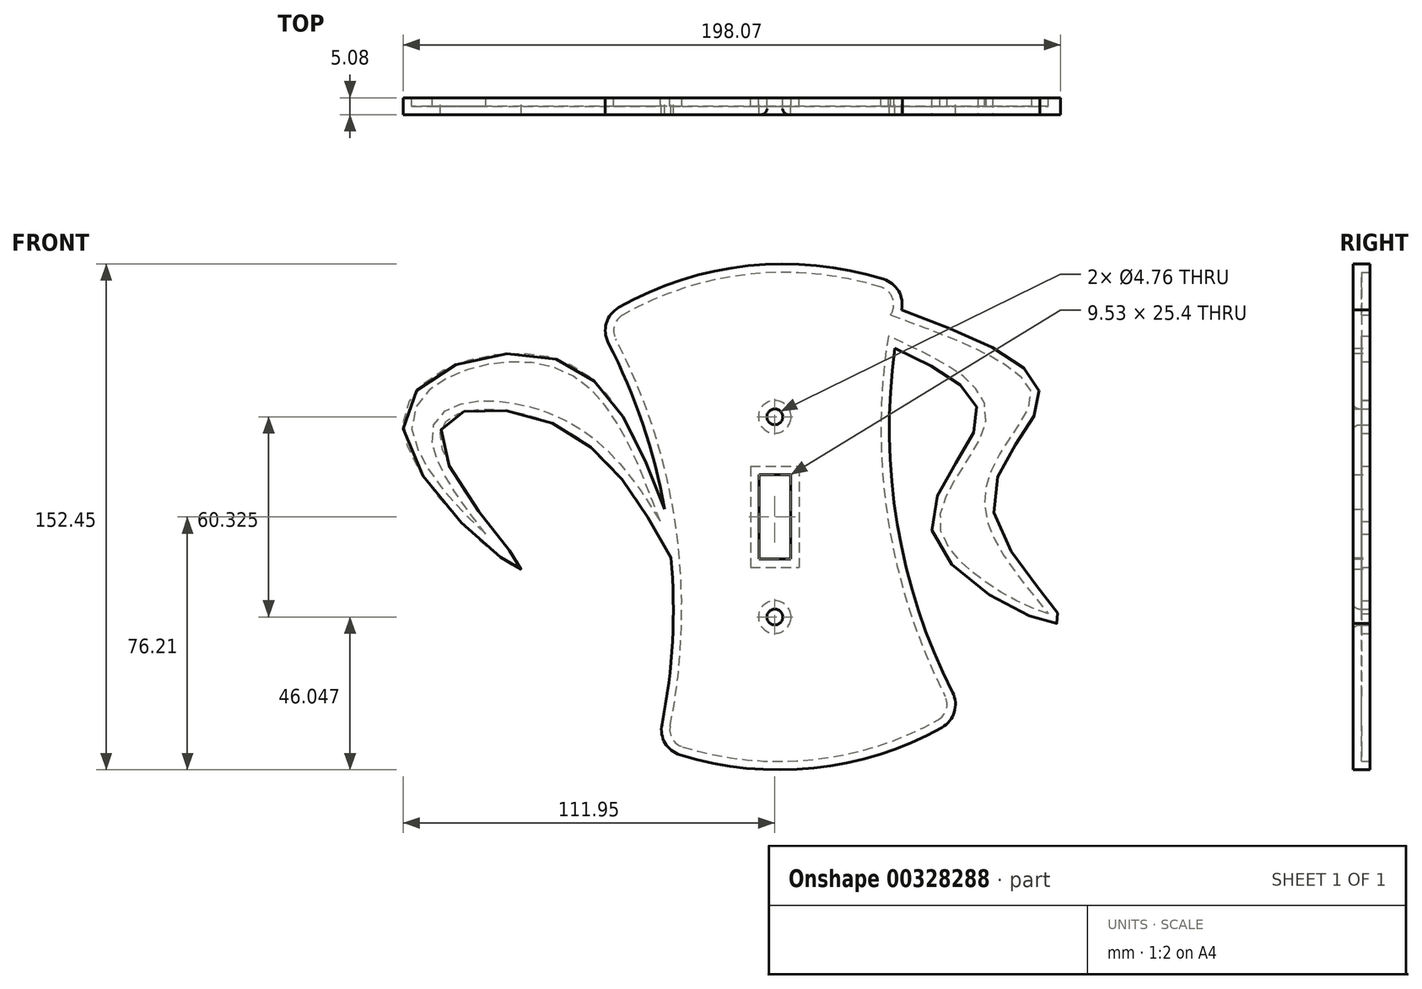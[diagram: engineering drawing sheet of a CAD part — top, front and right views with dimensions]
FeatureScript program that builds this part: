
annotation { "Feature Type Name" : "Feature", "Feature Type Description" : "" }
export const myFeature = defineFeature(function(context is Context, id is Id, definition is map)
    precondition{}
    {
        {
            var Q0;
            Q0=qCreatedBy(makeId("Front.planeOp"),FACE);
            var sketch = newSketch(context, id + "F0", { "sketchPlane" : qUnion([Q0])});
            skArc(sketch, "E0", {"start": v(-34, -62.51) * mm, "mid": v(-30.83, -37.47) * mm, "end": v(-31.28, -12.22) * mm});
            skArc(sketch, "E1", {"start": v(32.8, 71.63) * mm, "mid": v(-8, 75.67) * mm, "end": v(-47.03, 63.1) * mm});
            skArc(sketch, "E2", {"start": v(-28.56, -71.7) * mm, "mid": v(11.73, -75.66) * mm, "end": v(50.33, -63.43) * mm});
            skPoint(sketch, "E3.visualSharp", {"position": v(-35.5, -69.25) * mm});
            skArc(sketch, "E3.filletArc", {"start": v(-34, -62.51) * mm, "mid": v(-33.05, -68.15) * mm, "end": v(-28.56, -71.7) * mm});
            skPoint(sketch, "E4.visualSharp", {"position": v(57.01, -59.35) * mm});
            skArc(sketch, "E4.filletArc", {"start": v(50.33, -63.43) * mm, "mid": v(54.06, -58.8) * mm, "end": v(53.54, -52.86) * mm});
            skPoint(sketch, "E5.visualSharp", {"position": v(39.76, 69.16) * mm});
            skArc(sketch, "E5.filletArc", {"start": v(38.2, 62.4) * mm, "mid": v(37.28, 68.05) * mm, "end": v(32.8, 71.63) * mm});
            skPoint(sketch, "E6.visualSharp", {"position": v(-53.69, 58.96) * mm});
            skArc(sketch, "E6.filletArc", {"start": v(-47.03, 63.1) * mm, "mid": v(-50.73, 58.43) * mm, "end": v(-50.17, 52.5) * mm});
            skCircle(sketch, "E7", {"center": v(0, 30.16) * mm, "radius": 2.38 * mm});
            skCircle(sketch, "E8", {"center": v(0, -30.16) * mm, "radius": 2.38 * mm});
            skArc(sketch, "E9.trimOffspring", {"start": v(36.19, 50.82) * mm, "mid": v(36.9, -2.35) * mm, "end": v(53.54, -52.86) * mm});
            skArc(sketch, "E10.trimOffspring", {"start": v(-33.22, 2.38) * mm, "mid": v(-39.8, 28.09) * mm, "end": v(-50.17, 52.5) * mm});
            skLineSegment(sketch, "E11", {"start": v(0, 0) * mm, "end": v(-34, 0) * mm});
            skLineSegment(sketch, "E12.bottom", {"start": v(-4.76, 12.7) * mm, "end": v(4.76, 12.7) * mm});
            skLineSegment(sketch, "E12.top", {"start": v(-4.76, -12.7) * mm, "end": v(4.76, -12.7) * mm});
            skLineSegment(sketch, "E12.left", {"start": v(-4.76, 12.7) * mm, "end": v(-4.76, -12.7) * mm});
            skLineSegment(sketch, "E12.right", {"start": v(4.76, 12.7) * mm, "end": v(4.76, -12.7) * mm});
            skFitSpline(sketch, "E13", {"points": [v(-33.22, 2.38) * mm, v(-67.85, 48.13) * mm, v(-111.92, 26.99) * mm, v(-76.45, -15.65) * mm, v(-100.82, 24.48) * mm, v(-67.5, 28.42) * mm, v(-31.28, -12.22) * mm], "startDerivative": vector(-128.9, 340.6) * mm, "endDerivative": vector(158.19, -283.48) * mm});
            skFitSpline(sketch, "E14", {"points": [v(38.2, 62.4) * mm, v(79.78, 36.3) * mm, v(65.8, 2.38) * mm, v(85.87, -31.78) * mm, v(47.89, -5.98) * mm, v(61.15, 29.85) * mm, v(36.19, 50.82) * mm], "startDerivative": vector(339.25, -127.04) * mm, "endDerivative": vector(-257.01, 120.19) * mm});
            skSolve(sketch);
        }
        {
            var Q0;
            Q0=makeQuery(id+"F0.imprint","IMPRINT",FACE,{"disambiguationData":[TD([[makeQuery(id+"F0.imprint","IMPRINT",EDGE,{"derivedFrom":sQuery(id+"F0.wireOp",EDGE,"E0")}),-1.0]])]});
            extrude(context, id + "F1", {"entities" : qUnion([Q0]), "depth" : 5.08 * mm});
        }
        {
            var Q0;
            Q0=makeQuery(id+"F1.opExtrude","CAP_EDGE",EDGE,{"disambiguationData":[OSD([sQuery(id+"F0.wireOp",EDGE,"E7")])],"isStart":false});
            var Q1;
            Q1=makeQuery(id+"F1.opExtrude","CAP_EDGE",EDGE,{"disambiguationData":[OSD([sQuery(id+"F0.wireOp",EDGE,"E8")])],"isStart":false});
            fillet(context, id + "F2", {"entities" : qUnion([Q0, Q1]), "radius" : 1.78 * mm, "tangentPropagation" : true, "allowEdgeOverflow" : false});
        }
        {
            var Q0;
            Q0=makeQuery(id+"F1.opExtrude","CAP_FACE",FACE,{"disambiguationData":[OSD([sQuery(id+"F0.wireOp",EDGE,"E0"),sQuery(id+"F0.wireOp",EDGE,"6P8noCB4-dQS9-niCE-kcvC-e65ASGhALeeu"),sQuery(id+"F0.wireOp",EDGE,"E1"),sQuery(id+"F0.wireOp",EDGE,"E2"),sQuery(id+"F0.wireOp",EDGE,"E3.filletArc"),sQuery(id+"F0.wireOp",EDGE,"E4.filletArc"),sQuery(id+"F0.wireOp",EDGE,"E5.filletArc"),sQuery(id+"F0.wireOp",EDGE,"E6.filletArc"),sQuery(id+"F0.wireOp",EDGE,"E7"),sQuery(id+"F0.wireOp",EDGE,"E8"),sQuery(id+"F0.wireOp",EDGE,"e4c59e5b-64f9-48a5-89de-955b67e849d5"),sQuery(id+"F0.wireOp",EDGE,"E9.trimOffspring"),sQuery(id+"F0.wireOp",EDGE,"E10.trimOffspring"),sQuery(id+"F0.wireOp",EDGE,"a3041db4-6055-42ae-b1ec-9a864373a417"),sQuery(id+"F0.wireOp",EDGE,"c8798bba-adf1-4085-968a-abd4420d5c5a"),sQuery(id+"F0.wireOp",EDGE,"fdd86a6c-a444-4d6f-ab5d-d8b721dcd338.trimOffspring"),sQuery(id+"F0.wireOp",EDGE,"aa541cdf-7661-45fb-893d-a3c4a677e4ac"),sQuery(id+"F0.wireOp",EDGE,"fb5a7162-4551-47be-b8af-1cf4c87edb5e"),sQuery(id+"F0.wireOp",EDGE,"E12.bottom"),sQuery(id+"F0.wireOp",EDGE,"E12.top"),sQuery(id+"F0.wireOp",EDGE,"E12.left"),sQuery(id+"F0.wireOp",EDGE,"E12.right")])],"isStart":true});
            shell(context, id + "F3", {"entities" : qUnion([Q0]), "thickness" : 2.54 * mm});
        }
    });
